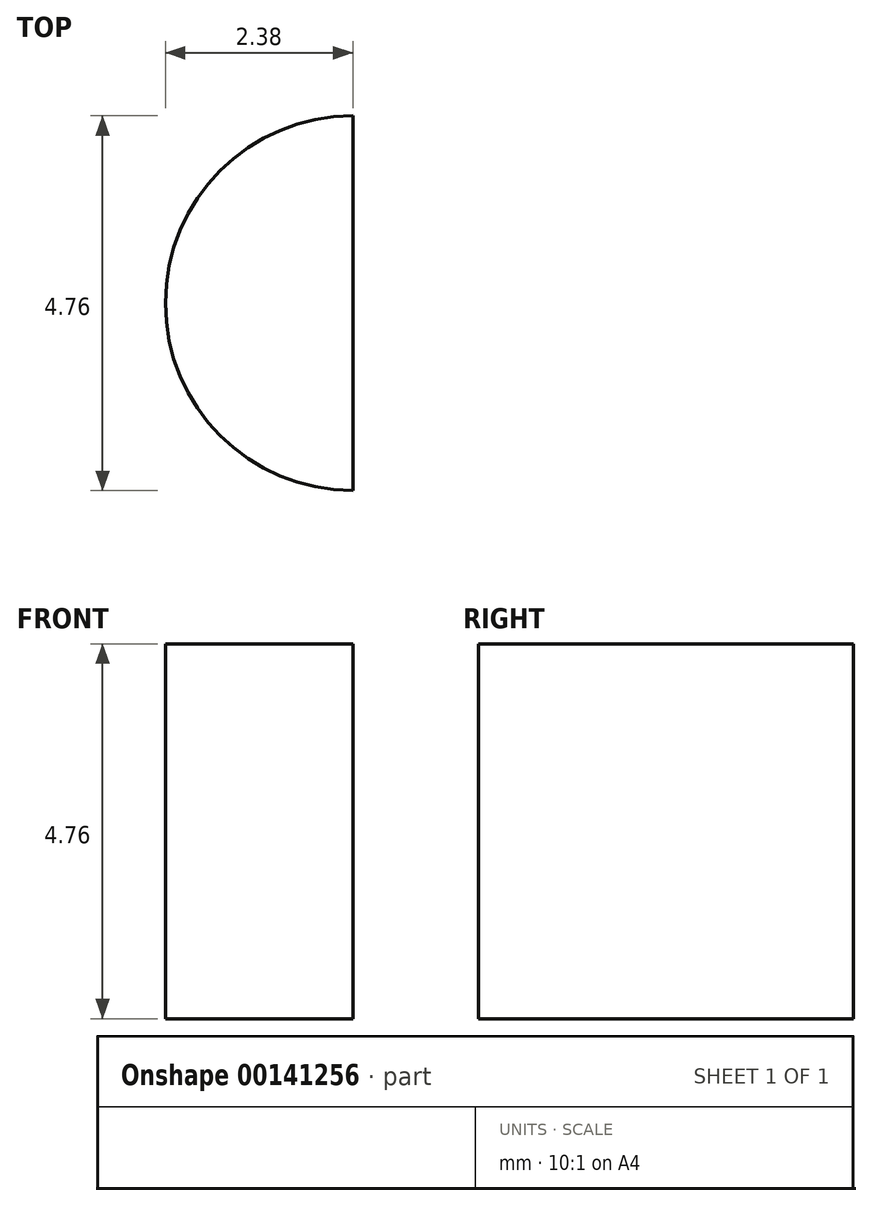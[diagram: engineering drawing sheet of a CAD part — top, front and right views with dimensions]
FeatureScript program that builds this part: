
annotation { "Feature Type Name" : "Feature", "Feature Type Description" : "" }
export const myFeature = defineFeature(function(context is Context, id is Id, definition is map)
    precondition{}
    {
        {
            var Q0;
            Q0=qCreatedBy(makeId("Top.planeOp"),FACE);
            var sketch = newSketch(context, id + "F0", { "sketchPlane" : qUnion([Q0])});
            skArc(sketch, "E0", {"start": v(0, 2.38) * mm, "mid": v(-2.38, 0) * mm, "end": v(0, -2.38) * mm});
            skLineSegment(sketch, "E1", {"start": v(0, 2.38) * mm, "end": v(0, -2.38) * mm});
            skPoint(sketch, "E2.orphan", {"position": v(0, 3.32) * mm});
            skSolve(sketch);
        }
        {
            var Q0;
            Q0=makeQuery(id+"F0.imprint","IMPRINT",FACE,{"disambiguationData":[TD([[makeQuery(id+"F0.imprint","IMPRINT",EDGE,{"derivedFrom":sQuery(id+"F0.wireOp",EDGE,"E0")}),1.0]])]});
            extrude(context, id + "F1", {"entities" : qUnion([Q0]), "depth" : 4.76 * mm});
        }
    });
